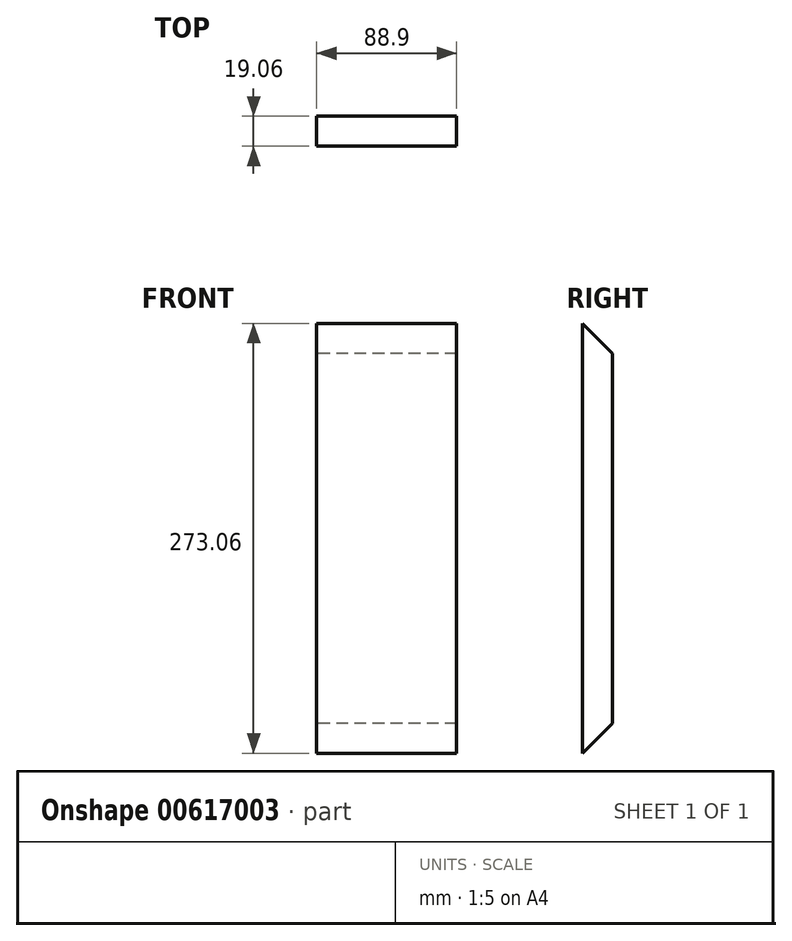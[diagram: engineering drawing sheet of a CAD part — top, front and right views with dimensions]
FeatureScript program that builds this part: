
annotation { "Feature Type Name" : "Feature", "Feature Type Description" : "" }
export const myFeature = defineFeature(function(context is Context, id is Id, definition is map)
    precondition{}
    {
        {
            var Q0;
            Q0=qCreatedBy(makeId("Right.planeOp"),FACE);
            var sketch = newSketch(context, id + "F0", { "sketchPlane" : qUnion([Q0])});
            skLineSegment(sketch, "E0.left", {"start": v(9.52, 117.48) * mm, "end": v(9.52, -117.48) * mm});
            skPoint(sketch, "E0.middle", {"position": v(0, 0) * mm});
            skLineSegment(sketch, "E1", {"start": v(-9.53, 136.53) * mm, "end": v(9.52, 117.48) * mm});
            skPoint(sketch, "E2.orphan", {"position": v(9.52, 136.52) * mm});
            skLineSegment(sketch, "E3", {"start": v(-9.53, -136.53) * mm, "end": v(9.52, -117.48) * mm});
            skPoint(sketch, "E0.top.start.orphan", {"position": v(9.53, -136.53) * mm});
            skLineSegment(sketch, "E4", {"start": v(-9.53, 136.53) * mm, "end": v(-9.53, 0) * mm});
            skLineSegment(sketch, "E5", {"start": v(-9.53, 0) * mm, "end": v(-9.53, -136.53) * mm});
            skSolve(sketch);
        }
        {
            var Q0;
            Q0=makeQuery(id+"F0.imprint","IMPRINT",FACE,{"disambiguationData":[TD([[makeQuery(id+"F0.imprint","IMPRINT",EDGE,{"derivedFrom":sQuery(id+"F0.wireOp",EDGE,"E0.left")}),-1.0]])]});
            extrude(context, id + "F1", {"entities" : qUnion([Q0]), "depth" : 88.9 * mm, "offsetDistance" : 25.4 * mm});
        }
    });
